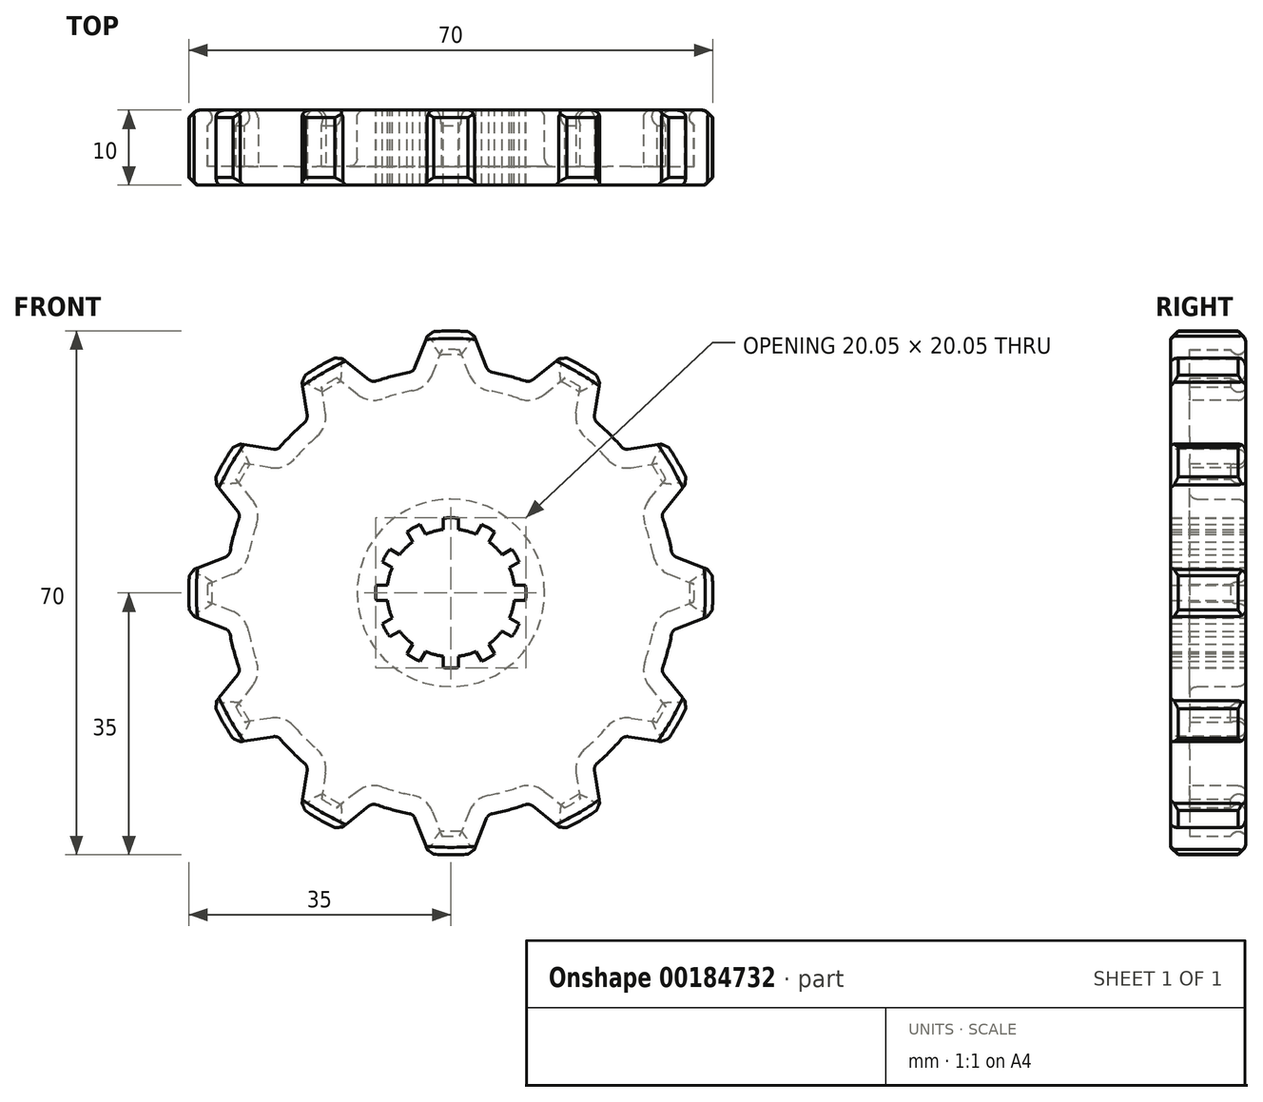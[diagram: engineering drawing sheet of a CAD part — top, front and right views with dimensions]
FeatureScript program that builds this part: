
annotation { "Feature Type Name" : "Feature", "Feature Type Description" : "" }
export const myFeature = defineFeature(function(context is Context, id is Id, definition is map)
    precondition{}
    {
        {
            var Q0;
            Q0=qCreatedBy(makeId("Front.planeOp"),FACE);
            var sketch = newSketch(context, id + "F0", { "sketchPlane" : qUnion([Q0])});
            skCircle(sketch, "E0", {"center": v(0, 0) * mm, "radius": 35 * mm});
            skSolve(sketch);
        }
        {
            var Q0;
            Q0=makeQuery(id+"F0.imprint","IMPRINT",FACE,{"disambiguationData":[TD([[makeQuery(id+"F0.imprint","IMPRINT",EDGE,{"derivedFrom":sQuery(id+"F0.wireOp",EDGE,"E0")}),1.0]])]});
            extrude(context, id + "F1", {"entities" : qUnion([Q0]), "depth" : 10 * mm});
        }
        {
            var Q0;
            Q0=makeQuery(id+"F1.opExtrude","CAP_FACE",FACE,{"disambiguationData":[OSD([sQuery(id+"F0.wireOp",EDGE,"E0")])],"isStart":false});
            var sketch = newSketch(context, id + "F2", { "sketchPlane" : qUnion([Q0])});
            skArc(sketch, "E1", {"start": v(29.48, 5.54) * mm, "mid": v(-30, 0) * mm, "end": v(29.48, -5.54) * mm});
            skLineSegment(sketch, "E2", {"start": v(0, 0) * mm, "end": v(37.5, 0) * mm, "construction": true});
            skLineSegment(sketch, "E3", {"start": v(30, 0) * mm, "end": v(30, 11.9) * mm, "construction": true});
            skLineSegment(sketch, "E4.0", {"start": v(0, 5) * mm, "end": v(37.5, 5) * mm, "construction": true});
            skLineSegment(sketch, "E5.0", {"start": v(0, -5) * mm, "end": v(37.5, -5) * mm, "construction": true});
            skLineSegment(sketch, "E6", {"start": v(30.1, 4.8) * mm, "end": v(34.87, 2.92) * mm});
            skLineSegment(sketch, "E7.MirrorCS", {"start": v(30.1, -4.8) * mm, "end": v(34.87, -2.92) * mm});
            skPoint(sketch, "E8.visualSharp", {"position": v(29.58, 5) * mm});
            skArc(sketch, "E8.filletArc", {"start": v(29.48, 5.54) * mm, "mid": v(29.7, 5.09) * mm, "end": v(30.1, 4.8) * mm});
            skPoint(sketch, "E9.visualSharp", {"position": v(29.58, -5) * mm});
            skArc(sketch, "E9.filletArc", {"start": v(30.1, -4.8) * mm, "mid": v(29.7, -5.09) * mm, "end": v(29.48, -5.54) * mm});
            skPoint(sketch, "E10.1.0", {"position": v(28.12, 10.46) * mm});
            skLineSegment(sketch, "E10.1.1", {"start": v(23.67, 19.2) * mm, "end": v(28.74, 19.97) * mm});
            skPoint(sketch, "E10.1.2", {"position": v(23.12, 19.12) * mm});
            skLineSegment(sketch, "E10.1.3", {"start": v(28.47, 10.9) * mm, "end": v(31.66, 14.9) * mm});
            skArc(sketch, "E10.1.4", {"start": v(22.76, 19.54) * mm, "mid": v(23.17, 19.26) * mm, "end": v(23.67, 19.2) * mm});
            skArc(sketch, "E10.1.5", {"start": v(28.47, 10.9) * mm, "mid": v(28.26, 10.44) * mm, "end": v(28.3, 9.94) * mm});
            skPoint(sketch, "E10.2.0", {"position": v(19.12, 23.12) * mm});
            skLineSegment(sketch, "E10.2.1", {"start": v(10.9, 28.47) * mm, "end": v(14.9, 31.66) * mm});
            skPoint(sketch, "E10.2.2", {"position": v(10.46, 28.12) * mm});
            skLineSegment(sketch, "E10.2.3", {"start": v(19.2, 23.67) * mm, "end": v(19.97, 28.74) * mm});
            skArc(sketch, "E10.2.4", {"start": v(9.94, 28.3) * mm, "mid": v(10.44, 28.26) * mm, "end": v(10.9, 28.47) * mm});
            skArc(sketch, "E10.2.5", {"start": v(19.2, 23.67) * mm, "mid": v(19.26, 23.17) * mm, "end": v(19.54, 22.76) * mm});
            skLineSegment(sketch, "E11.1.3.0", {"start": v(-4.8, 30.1) * mm, "end": v(-2.92, 34.87) * mm});
            skPoint(sketch, "E11.4.3.0", {"position": v(-5, 29.58) * mm});
            skLineSegment(sketch, "E11.5.3.0", {"start": v(4.8, 30.1) * mm, "end": v(2.92, 34.87) * mm});
            skArc(sketch, "E11.8.3.0", {"start": v(-5.54, 29.48) * mm, "mid": v(-5.09, 29.7) * mm, "end": v(-4.8, 30.1) * mm});
            skArc(sketch, "E11.12.3.0", {"start": v(4.8, 30.1) * mm, "mid": v(5.09, 29.7) * mm, "end": v(5.54, 29.48) * mm});
            skPoint(sketch, "E11.15.3.0", {"position": v(5, 29.58) * mm});
            skLineSegment(sketch, "E11.1.4.0", {"start": v(-19.2, 23.67) * mm, "end": v(-19.97, 28.74) * mm});
            skPoint(sketch, "E11.4.4.0", {"position": v(-19.12, 23.12) * mm});
            skLineSegment(sketch, "E11.5.4.0", {"start": v(-10.9, 28.47) * mm, "end": v(-14.9, 31.66) * mm});
            skArc(sketch, "E11.8.4.0", {"start": v(-19.54, 22.76) * mm, "mid": v(-19.26, 23.17) * mm, "end": v(-19.2, 23.67) * mm});
            skArc(sketch, "E11.12.4.0", {"start": v(-10.9, 28.47) * mm, "mid": v(-10.44, 28.26) * mm, "end": v(-9.94, 28.3) * mm});
            skPoint(sketch, "E11.15.4.0", {"position": v(-10.46, 28.12) * mm});
            skLineSegment(sketch, "E11.1.5.0", {"start": v(-28.47, 10.9) * mm, "end": v(-31.66, 14.9) * mm});
            skPoint(sketch, "E11.4.5.0", {"position": v(-28.12, 10.46) * mm});
            skLineSegment(sketch, "E11.5.5.0", {"start": v(-23.67, 19.2) * mm, "end": v(-28.74, 19.97) * mm});
            skArc(sketch, "E11.8.5.0", {"start": v(-28.3, 9.94) * mm, "mid": v(-28.26, 10.44) * mm, "end": v(-28.47, 10.9) * mm});
            skArc(sketch, "E11.12.5.0", {"start": v(-23.67, 19.2) * mm, "mid": v(-23.17, 19.26) * mm, "end": v(-22.76, 19.54) * mm});
            skPoint(sketch, "E11.15.5.0", {"position": v(-23.12, 19.12) * mm});
            skLineSegment(sketch, "E11.1.6.0", {"start": v(-30.1, -4.8) * mm, "end": v(-34.87, -2.92) * mm});
            skPoint(sketch, "E11.4.6.0", {"position": v(-29.58, -5) * mm});
            skLineSegment(sketch, "E11.5.6.0", {"start": v(-30.1, 4.8) * mm, "end": v(-34.87, 2.92) * mm});
            skArc(sketch, "E11.8.6.0", {"start": v(-29.48, -5.54) * mm, "mid": v(-29.7, -5.09) * mm, "end": v(-30.1, -4.8) * mm});
            skArc(sketch, "E11.12.6.0", {"start": v(-30.1, 4.8) * mm, "mid": v(-29.7, 5.09) * mm, "end": v(-29.48, 5.54) * mm});
            skPoint(sketch, "E11.15.6.0", {"position": v(-29.58, 5) * mm});
            skLineSegment(sketch, "E11.1.7.0", {"start": v(-23.67, -19.2) * mm, "end": v(-28.74, -19.97) * mm});
            skPoint(sketch, "E11.4.7.0", {"position": v(-23.12, -19.12) * mm});
            skLineSegment(sketch, "E11.5.7.0", {"start": v(-28.47, -10.9) * mm, "end": v(-31.66, -14.9) * mm});
            skArc(sketch, "E11.8.7.0", {"start": v(-22.76, -19.54) * mm, "mid": v(-23.17, -19.26) * mm, "end": v(-23.67, -19.2) * mm});
            skArc(sketch, "E11.12.7.0", {"start": v(-28.47, -10.9) * mm, "mid": v(-28.26, -10.44) * mm, "end": v(-28.3, -9.94) * mm});
            skPoint(sketch, "E11.15.7.0", {"position": v(-28.12, -10.46) * mm});
            skLineSegment(sketch, "E11.1.8.0", {"start": v(-10.9, -28.47) * mm, "end": v(-14.9, -31.66) * mm});
            skPoint(sketch, "E11.4.8.0", {"position": v(-10.46, -28.12) * mm});
            skLineSegment(sketch, "E11.5.8.0", {"start": v(-19.2, -23.67) * mm, "end": v(-19.97, -28.74) * mm});
            skArc(sketch, "E11.8.8.0", {"start": v(-9.94, -28.3) * mm, "mid": v(-10.44, -28.26) * mm, "end": v(-10.9, -28.47) * mm});
            skArc(sketch, "E11.12.8.0", {"start": v(-19.2, -23.67) * mm, "mid": v(-19.26, -23.17) * mm, "end": v(-19.54, -22.76) * mm});
            skPoint(sketch, "E11.15.8.0", {"position": v(-19.12, -23.12) * mm});
            skLineSegment(sketch, "E11.1.9.0", {"start": v(4.8, -30.1) * mm, "end": v(2.92, -34.87) * mm});
            skPoint(sketch, "E11.4.9.0", {"position": v(5, -29.58) * mm});
            skLineSegment(sketch, "E11.5.9.0", {"start": v(-4.8, -30.1) * mm, "end": v(-2.92, -34.87) * mm});
            skArc(sketch, "E11.8.9.0", {"start": v(5.54, -29.48) * mm, "mid": v(5.09, -29.7) * mm, "end": v(4.8, -30.1) * mm});
            skArc(sketch, "E11.12.9.0", {"start": v(-4.8, -30.1) * mm, "mid": v(-5.09, -29.7) * mm, "end": v(-5.54, -29.48) * mm});
            skPoint(sketch, "E11.15.9.0", {"position": v(-5, -29.58) * mm});
            skLineSegment(sketch, "E11.1.10.0", {"start": v(19.2, -23.67) * mm, "end": v(19.97, -28.74) * mm});
            skPoint(sketch, "E11.4.10.0", {"position": v(19.12, -23.12) * mm});
            skLineSegment(sketch, "E11.5.10.0", {"start": v(10.9, -28.47) * mm, "end": v(14.9, -31.66) * mm});
            skArc(sketch, "E11.8.10.0", {"start": v(19.54, -22.76) * mm, "mid": v(19.26, -23.17) * mm, "end": v(19.2, -23.67) * mm});
            skArc(sketch, "E11.12.10.0", {"start": v(10.9, -28.47) * mm, "mid": v(10.44, -28.26) * mm, "end": v(9.94, -28.3) * mm});
            skPoint(sketch, "E11.15.10.0", {"position": v(10.46, -28.12) * mm});
            skLineSegment(sketch, "E11.1.11.0", {"start": v(28.47, -10.9) * mm, "end": v(31.66, -14.9) * mm});
            skPoint(sketch, "E11.4.11.0", {"position": v(28.12, -10.46) * mm});
            skLineSegment(sketch, "E11.5.11.0", {"start": v(23.67, -19.2) * mm, "end": v(28.74, -19.97) * mm});
            skArc(sketch, "E11.8.11.0", {"start": v(28.3, -9.94) * mm, "mid": v(28.26, -10.44) * mm, "end": v(28.47, -10.9) * mm});
            skArc(sketch, "E11.12.11.0", {"start": v(23.67, -19.2) * mm, "mid": v(23.17, -19.26) * mm, "end": v(22.76, -19.54) * mm});
            skPoint(sketch, "E11.15.11.0", {"position": v(23.12, -19.12) * mm});
            skSolve(sketch);
        }
        {
            var Q0;
            {var subQ1=sQuery(id+"F2.wireOp",EDGE,"E7.MirrorCS");Q0=makeQuery(id+"F2.imprint","IMPRINT",FACE,{"disambiguationData":[TD([[makeQuery(id+"F2.imprint","IMPRINT",EDGE,{"derivedFrom":subQ1}),-1.0]])]});}
            var Q1;
            {var subQ1=sQuery(id+"F2.wireOp",EDGE,"E11.1.10.0");Q1=makeQuery(id+"F2.imprint","IMPRINT",FACE,{"disambiguationData":[TD([[makeQuery(id+"F2.imprint","IMPRINT",EDGE,{"derivedFrom":subQ1}),1.0]])]});}
            var Q2;
            {var subQ2=sQuery(id+"F2.wireOp",EDGE,"E11.1.9.0");Q2=makeQuery(id+"F2.imprint","IMPRINT",FACE,{"disambiguationData":[TD([[makeQuery(id+"F2.imprint","IMPRINT",EDGE,{"derivedFrom":subQ2}),1.0]])]});}
            var Q3;
            {var subQ2=sQuery(id+"F2.wireOp",EDGE,"E11.1.8.0");Q3=makeQuery(id+"F2.imprint","IMPRINT",FACE,{"disambiguationData":[TD([[makeQuery(id+"F2.imprint","IMPRINT",EDGE,{"derivedFrom":subQ2}),1.0]])]});}
            var Q4;
            {var subQ1=sQuery(id+"F2.wireOp",EDGE,"E11.1.7.0");Q4=makeQuery(id+"F2.imprint","IMPRINT",FACE,{"disambiguationData":[TD([[makeQuery(id+"F2.imprint","IMPRINT",EDGE,{"derivedFrom":subQ1}),1.0]])]});}
            var Q5;
            {var subQ2=sQuery(id+"F2.wireOp",EDGE,"E11.1.6.0");Q5=makeQuery(id+"F2.imprint","IMPRINT",FACE,{"disambiguationData":[TD([[makeQuery(id+"F2.imprint","IMPRINT",EDGE,{"derivedFrom":subQ2}),1.0]])]});}
            var Q6;
            {var subQ1=sQuery(id+"F2.wireOp",EDGE,"E11.1.5.0");Q6=makeQuery(id+"F2.imprint","IMPRINT",FACE,{"disambiguationData":[TD([[makeQuery(id+"F2.imprint","IMPRINT",EDGE,{"derivedFrom":subQ1}),1.0]])]});}
            var Q7;
            {var subQ1=sQuery(id+"F2.wireOp",EDGE,"E11.1.4.0");Q7=makeQuery(id+"F2.imprint","IMPRINT",FACE,{"disambiguationData":[TD([[makeQuery(id+"F2.imprint","IMPRINT",EDGE,{"derivedFrom":subQ1}),1.0]])]});}
            var Q8;
            {var subQ2=sQuery(id+"F2.wireOp",EDGE,"E11.1.3.0");Q8=makeQuery(id+"F2.imprint","IMPRINT",FACE,{"disambiguationData":[TD([[makeQuery(id+"F2.imprint","IMPRINT",EDGE,{"derivedFrom":subQ2}),1.0]])]});}
            var Q9;
            {var subQ1=sQuery(id+"F2.wireOp",EDGE,"E10.2.1");Q9=makeQuery(id+"F2.imprint","IMPRINT",FACE,{"disambiguationData":[TD([[makeQuery(id+"F2.imprint","IMPRINT",EDGE,{"derivedFrom":subQ1}),1.0]])]});}
            var Q10;
            {var subQ1=sQuery(id+"F2.wireOp",EDGE,"E10.1.1");Q10=makeQuery(id+"F2.imprint","IMPRINT",FACE,{"disambiguationData":[TD([[makeQuery(id+"F2.imprint","IMPRINT",EDGE,{"derivedFrom":subQ1}),1.0]])]});}
            var Q11;
            {var subQ2=sQuery(id+"F2.wireOp",EDGE,"E6");Q11=makeQuery(id+"F2.imprint","IMPRINT",FACE,{"disambiguationData":[TD([[makeQuery(id+"F2.imprint","IMPRINT",EDGE,{"derivedFrom":subQ2}),1.0]])]});}
            extrude(context, id + "F3", {"entities" : qUnion([Q0, Q1, Q2, Q3, Q4, Q5, Q6, Q7, Q8, Q9, Q10, Q11]), "operationType" : NewBodyOperationType.REMOVE, "endBound" : BoundingType.THROUGH_ALL, "oppositeDirection" : true, "depth" : 25 * mm});
        }
        {
            var Q0;
            {var subQ0=sQuery(id+"F0.wireOp",EDGE,"E0");Q0=makeQuery(id+"F3.boolean.opBoolean","SPLIT",FACE,{"disambiguationData":[TD([makeQuery(id+"F3.opExtrude","SWEPT_FACE",FACE,{"disambiguationData":[OSD([sQuery(id+"F2.wireOp",EDGE,"E6")])]})])],"derivedFrom":makeQuery(id+"F1.opExtrude","SWEPT_FACE",FACE,{"disambiguationData":[OSD([subQ0])]})});}
            var Q1;
            {var subQ0=sQuery(id+"F0.wireOp",EDGE,"E0");Q1=makeQuery(id+"F3.boolean.opBoolean","SPLIT",FACE,{"disambiguationData":[TD([makeQuery(id+"F3.opExtrude","SWEPT_FACE",FACE,{"disambiguationData":[OSD([sQuery(id+"F2.wireOp",EDGE,"E11.1.11.0")])]})])],"derivedFrom":makeQuery(id+"F1.opExtrude","SWEPT_FACE",FACE,{"disambiguationData":[OSD([subQ0])]})});}
            var Q2;
            {var subQ0=sQuery(id+"F0.wireOp",EDGE,"E0");Q2=makeQuery(id+"F3.boolean.opBoolean","SPLIT",FACE,{"disambiguationData":[TD([makeQuery(id+"F3.opExtrude","SWEPT_FACE",FACE,{"disambiguationData":[OSD([sQuery(id+"F2.wireOp",EDGE,"E11.1.10.0")])]})])],"derivedFrom":makeQuery(id+"F1.opExtrude","SWEPT_FACE",FACE,{"disambiguationData":[OSD([subQ0])]})});}
            var Q3;
            {var subQ0=sQuery(id+"F0.wireOp",EDGE,"E0");Q3=makeQuery(id+"F3.boolean.opBoolean","SPLIT",FACE,{"disambiguationData":[TD([makeQuery(id+"F3.opExtrude","SWEPT_FACE",FACE,{"disambiguationData":[OSD([sQuery(id+"F2.wireOp",EDGE,"E11.1.9.0")])]})])],"derivedFrom":makeQuery(id+"F1.opExtrude","SWEPT_FACE",FACE,{"disambiguationData":[OSD([subQ0])]})});}
            var Q4;
            {var subQ0=sQuery(id+"F0.wireOp",EDGE,"E0");Q4=makeQuery(id+"F3.boolean.opBoolean","SPLIT",FACE,{"disambiguationData":[TD([makeQuery(id+"F3.opExtrude","SWEPT_FACE",FACE,{"disambiguationData":[OSD([sQuery(id+"F2.wireOp",EDGE,"E11.1.8.0")])]})])],"derivedFrom":makeQuery(id+"F1.opExtrude","SWEPT_FACE",FACE,{"disambiguationData":[OSD([subQ0])]})});}
            var Q5;
            {var subQ0=sQuery(id+"F0.wireOp",EDGE,"E0");Q5=makeQuery(id+"F3.boolean.opBoolean","SPLIT",FACE,{"disambiguationData":[TD([makeQuery(id+"F3.opExtrude","SWEPT_FACE",FACE,{"disambiguationData":[OSD([sQuery(id+"F2.wireOp",EDGE,"E11.1.7.0")])]})])],"derivedFrom":makeQuery(id+"F1.opExtrude","SWEPT_FACE",FACE,{"disambiguationData":[OSD([subQ0])]})});}
            var Q6;
            {var subQ0=sQuery(id+"F0.wireOp",EDGE,"E0");Q6=makeQuery(id+"F3.boolean.opBoolean","SPLIT",FACE,{"disambiguationData":[TD([makeQuery(id+"F3.opExtrude","SWEPT_FACE",FACE,{"disambiguationData":[OSD([sQuery(id+"F2.wireOp",EDGE,"E11.1.6.0")])]})])],"derivedFrom":makeQuery(id+"F1.opExtrude","SWEPT_FACE",FACE,{"disambiguationData":[OSD([subQ0])]})});}
            var Q7;
            {var subQ0=sQuery(id+"F0.wireOp",EDGE,"E0");Q7=makeQuery(id+"F3.boolean.opBoolean","SPLIT",FACE,{"disambiguationData":[TD([makeQuery(id+"F3.opExtrude","SWEPT_FACE",FACE,{"disambiguationData":[OSD([sQuery(id+"F2.wireOp",EDGE,"E11.1.5.0")])]})])],"derivedFrom":makeQuery(id+"F1.opExtrude","SWEPT_FACE",FACE,{"disambiguationData":[OSD([subQ0])]})});}
            var Q8;
            {var subQ0=sQuery(id+"F0.wireOp",EDGE,"E0");Q8=makeQuery(id+"F3.boolean.opBoolean","SPLIT",FACE,{"disambiguationData":[TD([makeQuery(id+"F3.opExtrude","SWEPT_FACE",FACE,{"disambiguationData":[OSD([sQuery(id+"F2.wireOp",EDGE,"E11.1.4.0")])]})])],"derivedFrom":makeQuery(id+"F1.opExtrude","SWEPT_FACE",FACE,{"disambiguationData":[OSD([subQ0])]})});}
            var Q9;
            {var subQ0=sQuery(id+"F0.wireOp",EDGE,"E0");Q9=makeQuery(id+"F3.boolean.opBoolean","SPLIT",FACE,{"disambiguationData":[TD([makeQuery(id+"F3.opExtrude","SWEPT_FACE",FACE,{"disambiguationData":[OSD([sQuery(id+"F2.wireOp",EDGE,"E11.1.3.0")])]})])],"derivedFrom":makeQuery(id+"F1.opExtrude","SWEPT_FACE",FACE,{"disambiguationData":[OSD([subQ0])]})});}
            var Q10;
            {var subQ0=sQuery(id+"F0.wireOp",EDGE,"E0");Q10=makeQuery(id+"F3.boolean.opBoolean","SPLIT",FACE,{"disambiguationData":[TD([makeQuery(id+"F3.opExtrude","SWEPT_FACE",FACE,{"disambiguationData":[OSD([sQuery(id+"F2.wireOp",EDGE,"E10.2.1")])]})])],"derivedFrom":makeQuery(id+"F1.opExtrude","SWEPT_FACE",FACE,{"disambiguationData":[OSD([subQ0])]})});}
            var Q11;
            {var subQ0=sQuery(id+"F0.wireOp",EDGE,"E0");Q11=makeQuery(id+"F3.boolean.opBoolean","SPLIT",FACE,{"disambiguationData":[TD([makeQuery(id+"F3.opExtrude","SWEPT_FACE",FACE,{"disambiguationData":[OSD([sQuery(id+"F2.wireOp",EDGE,"E10.1.1")])]})])],"derivedFrom":makeQuery(id+"F1.opExtrude","SWEPT_FACE",FACE,{"disambiguationData":[OSD([subQ0])]})});}
            chamfer(context, id + "F4", {"entities" : qUnion([Q0, Q1, Q2, Q3, Q4, Q5, Q6, Q7, Q8, Q9, Q10, Q11]), "width" : 1 * mm, "tangentPropagation" : true});
        }
        {
            var Q0;
            Q0=makeQuery(id+"F1.opExtrude","CAP_FACE",FACE,{"disambiguationData":[OSD([sQuery(id+"F0.wireOp",EDGE,"E0")])],"isStart":true});
            var sketch = newSketch(context, id + "F5", { "sketchPlane" : qUnion([Q0])});
            skCircle(sketch, "E12", {"center": v(0, 0) * mm, "radius": 10.03 * mm});
            skLineSegment(sketch, "E13.0", {"start": v(1, 8.47) * mm, "end": v(1, 10) * mm});
            skLineSegment(sketch, "E14.0", {"start": v(-1, 8.47) * mm, "end": v(-1, 10) * mm});
            skCircle(sketch, "E15.0", {"center": v(0, 0) * mm, "radius": 8.53 * mm});
            skLineSegment(sketch, "E16.1.0", {"start": v(-5.1, 6.83) * mm, "end": v(-5.87, 8.16) * mm});
            skLineSegment(sketch, "E16.1.1", {"start": v(-3.37, 7.83) * mm, "end": v(-4.13, 9.16) * mm});
            skLineSegment(sketch, "E16.2.0", {"start": v(-7.83, 3.37) * mm, "end": v(-9.16, 4.13) * mm});
            skLineSegment(sketch, "E16.2.1", {"start": v(-6.83, 5.1) * mm, "end": v(-8.16, 5.87) * mm});
            skLineSegment(sketch, "E17.1.3.0", {"start": v(-8.47, -1) * mm, "end": v(-10, -1) * mm});
            skLineSegment(sketch, "E17.3.3.0", {"start": v(-8.47, 1) * mm, "end": v(-10, 1) * mm});
            skLineSegment(sketch, "E17.1.4.0", {"start": v(-6.83, -5.1) * mm, "end": v(-8.16, -5.87) * mm});
            skLineSegment(sketch, "E17.3.4.0", {"start": v(-7.83, -3.37) * mm, "end": v(-9.16, -4.13) * mm});
            skLineSegment(sketch, "E17.1.5.0", {"start": v(-3.37, -7.83) * mm, "end": v(-4.13, -9.16) * mm});
            skLineSegment(sketch, "E17.3.5.0", {"start": v(-5.1, -6.83) * mm, "end": v(-5.87, -8.16) * mm});
            skLineSegment(sketch, "E18.1.6.0", {"start": v(1, -8.47) * mm, "end": v(1, -10) * mm});
            skLineSegment(sketch, "E18.3.6.0", {"start": v(-1, -8.47) * mm, "end": v(-1, -10) * mm});
            skLineSegment(sketch, "E18.1.7.0", {"start": v(5.1, -6.83) * mm, "end": v(5.87, -8.16) * mm});
            skLineSegment(sketch, "E18.3.7.0", {"start": v(3.37, -7.83) * mm, "end": v(4.13, -9.16) * mm});
            skLineSegment(sketch, "E18.1.8.0", {"start": v(7.83, -3.37) * mm, "end": v(9.16, -4.13) * mm});
            skLineSegment(sketch, "E18.3.8.0", {"start": v(6.83, -5.1) * mm, "end": v(8.16, -5.87) * mm});
            skLineSegment(sketch, "E18.1.9.0", {"start": v(8.47, 1) * mm, "end": v(10, 1) * mm});
            skLineSegment(sketch, "E18.3.9.0", {"start": v(8.47, -1) * mm, "end": v(10, -1) * mm});
            skLineSegment(sketch, "E18.1.10.0", {"start": v(6.83, 5.1) * mm, "end": v(8.16, 5.87) * mm});
            skLineSegment(sketch, "E18.3.10.0", {"start": v(7.83, 3.37) * mm, "end": v(9.16, 4.13) * mm});
            skLineSegment(sketch, "E18.1.11.0", {"start": v(3.37, 7.83) * mm, "end": v(4.13, 9.16) * mm});
            skLineSegment(sketch, "E18.3.11.0", {"start": v(5.1, 6.83) * mm, "end": v(5.87, 8.16) * mm});
            skSolve(sketch);
        }
        {
            var Q0;
            {var subQ0=sQuery(id+"F5.wireOp",EDGE,"E17.3.5.0");var subQ1=sQuery(id+"F5.wireOp",EDGE,"E12");var subQ2=makeQuery(id+"F5.imprint","INTERSECT",VERTEX,{"derivedFrom":[subQ1,subQ0]});Q0=makeQuery(id+"F5.imprint","IMPRINT",FACE,{"disambiguationData":[TD([[makeQuery(id+"F5.imprint","IMPRINT",EDGE,{"disambiguationData":[TD([[subQ2,-1.0]])],"derivedFrom":subQ1}),1.0]])]});}
            var Q1;
            {var subQ0=sQuery(id+"F5.wireOp",EDGE,"E18.3.6.0");var subQ1=sQuery(id+"F5.wireOp",EDGE,"E12");var subQ2=makeQuery(id+"F5.imprint","INTERSECT",VERTEX,{"derivedFrom":[subQ1,subQ0]});Q1=makeQuery(id+"F5.imprint","IMPRINT",FACE,{"disambiguationData":[TD([[makeQuery(id+"F5.imprint","IMPRINT",EDGE,{"disambiguationData":[TD([[subQ2,-1.0]])],"derivedFrom":subQ1}),1.0]])]});}
            var Q2;
            {var subQ0=sQuery(id+"F5.wireOp",EDGE,"E18.3.7.0");var subQ1=sQuery(id+"F5.wireOp",EDGE,"E12");var subQ2=makeQuery(id+"F5.imprint","INTERSECT",VERTEX,{"derivedFrom":[subQ1,subQ0]});Q2=makeQuery(id+"F5.imprint","IMPRINT",FACE,{"disambiguationData":[TD([[makeQuery(id+"F5.imprint","IMPRINT",EDGE,{"disambiguationData":[TD([[subQ2,-1.0]])],"derivedFrom":subQ1}),1.0]])]});}
            var Q3;
            {var subQ0=sQuery(id+"F5.wireOp",EDGE,"E18.3.8.0");var subQ1=sQuery(id+"F5.wireOp",EDGE,"E12");var subQ2=makeQuery(id+"F5.imprint","INTERSECT",VERTEX,{"derivedFrom":[subQ1,subQ0]});Q3=makeQuery(id+"F5.imprint","IMPRINT",FACE,{"disambiguationData":[TD([[makeQuery(id+"F5.imprint","IMPRINT",EDGE,{"disambiguationData":[TD([[subQ2,-1.0]])],"derivedFrom":subQ1}),1.0]])]});}
            var Q4;
            {var subQ0=sQuery(id+"F5.wireOp",EDGE,"E18.1.9.0");var subQ1=sQuery(id+"F5.wireOp",EDGE,"E12");var subQ2=makeQuery(id+"F5.imprint","INTERSECT",VERTEX,{"derivedFrom":[subQ1,subQ0]});Q4=makeQuery(id+"F5.imprint","IMPRINT",FACE,{"disambiguationData":[TD([[makeQuery(id+"F5.imprint","IMPRINT",EDGE,{"disambiguationData":[TD([[subQ2,1.0]])],"derivedFrom":subQ1}),1.0]])]});}
            var Q5;
            {var subQ0=sQuery(id+"F5.wireOp",EDGE,"E18.3.10.0");var subQ1=sQuery(id+"F5.wireOp",EDGE,"E12");var subQ2=makeQuery(id+"F5.imprint","INTERSECT",VERTEX,{"derivedFrom":[subQ1,subQ0]});Q5=makeQuery(id+"F5.imprint","IMPRINT",FACE,{"disambiguationData":[TD([[makeQuery(id+"F5.imprint","IMPRINT",EDGE,{"disambiguationData":[TD([[subQ2,-1.0]])],"derivedFrom":subQ1}),1.0]])]});}
            var Q6;
            {var subQ0=sQuery(id+"F5.wireOp",EDGE,"E18.3.11.0");var subQ1=sQuery(id+"F5.wireOp",EDGE,"E12");var subQ2=makeQuery(id+"F5.imprint","INTERSECT",VERTEX,{"derivedFrom":[subQ1,subQ0]});Q6=makeQuery(id+"F5.imprint","IMPRINT",FACE,{"disambiguationData":[TD([[makeQuery(id+"F5.imprint","IMPRINT",EDGE,{"disambiguationData":[TD([[subQ2,-1.0]])],"derivedFrom":subQ1}),1.0]])]});}
            var Q7;
            {var subQ0=sQuery(id+"F5.wireOp",EDGE,"E13.0");var subQ1=sQuery(id+"F5.wireOp",EDGE,"E12");var subQ2=makeQuery(id+"F5.imprint","INTERSECT",VERTEX,{"derivedFrom":[subQ1,subQ0]});Q7=makeQuery(id+"F5.imprint","IMPRINT",FACE,{"disambiguationData":[TD([[makeQuery(id+"F5.imprint","IMPRINT",EDGE,{"disambiguationData":[TD([[subQ2,-1.0]])],"derivedFrom":subQ1}),1.0]])]});}
            var Q8;
            {var subQ0=sQuery(id+"F5.wireOp",EDGE,"E16.1.1");var subQ1=sQuery(id+"F5.wireOp",EDGE,"E12");var subQ2=makeQuery(id+"F5.imprint","INTERSECT",VERTEX,{"derivedFrom":[subQ1,subQ0]});Q8=makeQuery(id+"F5.imprint","IMPRINT",FACE,{"disambiguationData":[TD([[makeQuery(id+"F5.imprint","IMPRINT",EDGE,{"disambiguationData":[TD([[subQ2,-1.0]])],"derivedFrom":subQ1}),1.0]])]});}
            var Q9;
            {var subQ0=sQuery(id+"F5.wireOp",EDGE,"E17.3.4.0");var subQ1=sQuery(id+"F5.wireOp",EDGE,"E12");var subQ2=makeQuery(id+"F5.imprint","INTERSECT",VERTEX,{"derivedFrom":[subQ1,subQ0]});Q9=makeQuery(id+"F5.imprint","IMPRINT",FACE,{"disambiguationData":[TD([[makeQuery(id+"F5.imprint","IMPRINT",EDGE,{"disambiguationData":[TD([[subQ2,-1.0]])],"derivedFrom":subQ1}),1.0]])]});}
            var Q10;
            {var subQ0=sQuery(id+"F5.wireOp",EDGE,"E17.3.3.0");var subQ1=sQuery(id+"F5.wireOp",EDGE,"E12");var subQ2=makeQuery(id+"F5.imprint","INTERSECT",VERTEX,{"derivedFrom":[subQ1,subQ0]});Q10=makeQuery(id+"F5.imprint","IMPRINT",FACE,{"disambiguationData":[TD([[makeQuery(id+"F5.imprint","IMPRINT",EDGE,{"disambiguationData":[TD([[subQ2,-1.0]])],"derivedFrom":subQ1}),1.0]])]});}
            var Q11;
            {var subQ0=sQuery(id+"F5.wireOp",EDGE,"E16.2.1");var subQ1=sQuery(id+"F5.wireOp",EDGE,"E12");var subQ2=makeQuery(id+"F5.imprint","INTERSECT",VERTEX,{"derivedFrom":[subQ1,subQ0]});Q11=makeQuery(id+"F5.imprint","IMPRINT",FACE,{"disambiguationData":[TD([[makeQuery(id+"F5.imprint","IMPRINT",EDGE,{"disambiguationData":[TD([[subQ2,-1.0]])],"derivedFrom":subQ1}),1.0]])]});}
            var Q12;
            {var subQ0=sQuery(id+"F5.wireOp",EDGE,"E15.0");var subQ4=makeQuery(id+"F5.imprint","INTERSECT",VERTEX,{"derivedFrom":[subQ0,sQuery(id+"F5.wireOp",EDGE,"E18.1.9.0")]});Q12=makeQuery(id+"F5.imprint","IMPRINT",FACE,{"disambiguationData":[TD([[makeQuery(id+"F5.imprint","IMPRINT",EDGE,{"disambiguationData":[TD([[subQ4,-1.0]])],"derivedFrom":subQ0}),1.0]])]});}
            extrude(context, id + "F6", {"entities" : qUnion([Q0, Q1, Q2, Q3, Q4, Q5, Q6, Q7, Q8, Q9, Q10, Q11, Q12]), "operationType" : NewBodyOperationType.REMOVE, "endBound" : BoundingType.THROUGH_ALL, "oppositeDirection" : true, "depth" : 25 * mm});
        }
        {
            var Q0;
            Q0=makeQuery(id+"F1.opExtrude","CAP_FACE",FACE,{"disambiguationData":[OSD([sQuery(id+"F0.wireOp",EDGE,"E0")])],"isStart":true});
            shell(context, id + "F7", {"entities" : qUnion([Q0]), "thickness" : 2.5 * mm});
        }
        {
            var Q0;
            Q0=makeQuery(id+"F1.opExtrude","CAP_FACE",FACE,{"disambiguationData":[OSD([sQuery(id+"F0.wireOp",EDGE,"E0")])],"isStart":true});
            fillet(context, id + "F8", {"entities" : qUnion([Q0]), "radius" : 1 * mm, "tangentPropagation" : true, "allowEdgeOverflow" : false});
        }
        {
            var Q0;
            Q0=makeQuery(id+"F7.opShell","OFFSET_EDGE",EDGE,{"disambiguationData":[OSD([sQuery(id+"F5.wireOp",EDGE,"E12")])]});
            var Q1;
            Q1=makeQuery(id+"F7.opShell","OFFSET_EDGE",EDGE,{"disambiguationData":[OSD([sQuery(id+"F0.wireOp",EDGE,"E0"),sQuery(id+"F5.wireOp",EDGE,"E12")])]});
            fillet(context, id + "F9", {"entities" : qUnion([Q0, Q1]), "radius" : 1 * mm, "tangentPropagation" : true, "allowEdgeOverflow" : false});
        }
    });
